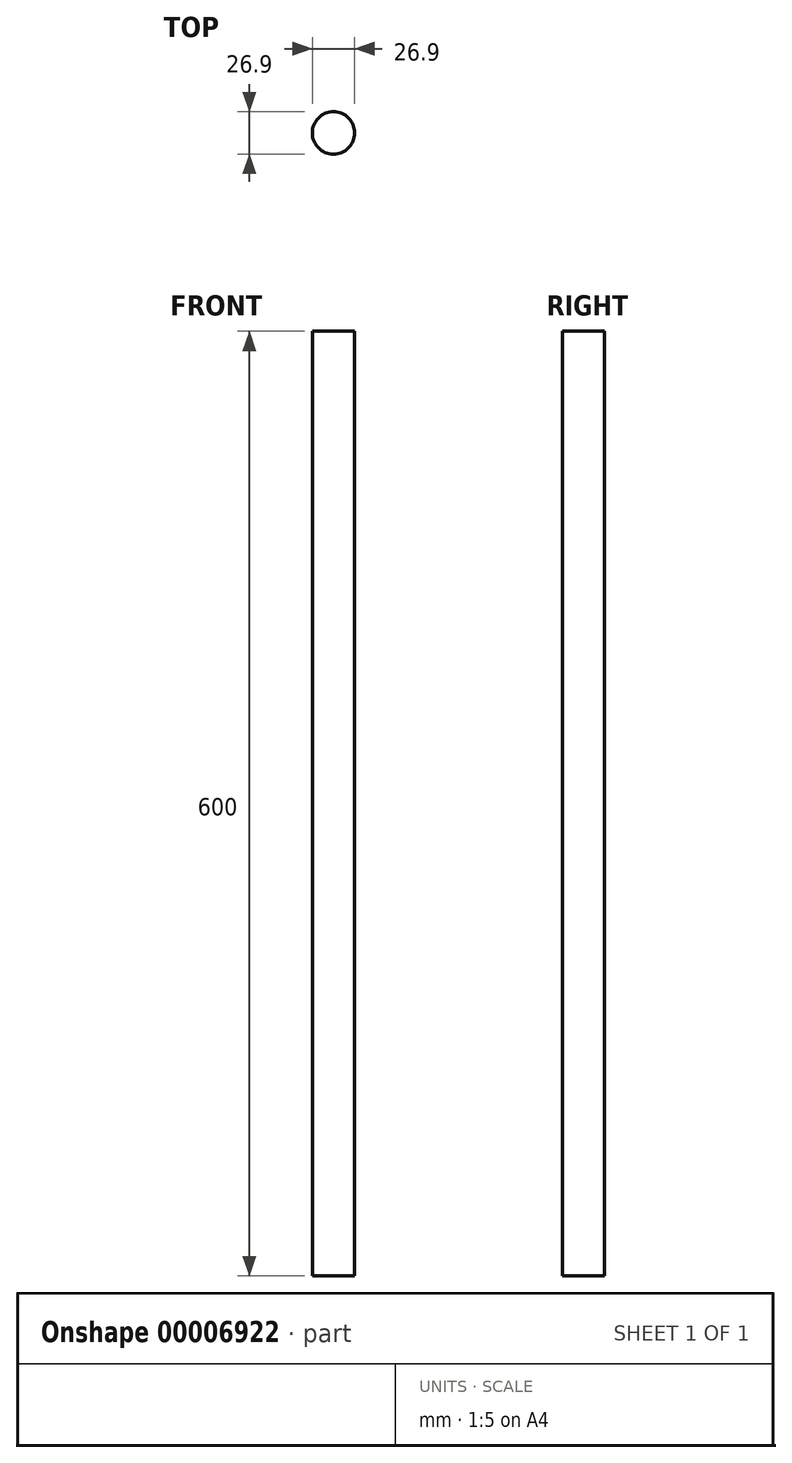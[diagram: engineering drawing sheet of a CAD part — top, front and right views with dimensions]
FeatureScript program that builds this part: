
annotation { "Feature Type Name" : "Feature", "Feature Type Description" : "" }
export const myFeature = defineFeature(function(context is Context, id is Id, definition is map)
    precondition{}
    {
        {
            var Q0;
            Q0=qCreatedBy(makeId("Top.planeOp"),FACE);
            var sketch = newSketch(context, id + "F0", { "sketchPlane" : qUnion([Q0])});
            skCircle(sketch, "E0", {"center": v(0, 0) * mm, "radius": 13.45 * mm});
            skSolve(sketch);
        }
        {
            var Q0;
            Q0=makeQuery(id+"F0.imprint","IMPRINT",FACE,{"disambiguationData":[TD([[makeQuery(id+"F0.imprint","IMPRINT",EDGE,{"derivedFrom":sQuery(id+"F0.wireOp",EDGE,"E0")}),1.0]])]});
            extrude(context, id + "F1", {"entities" : qUnion([Q0]), "depth" : (600) * mm});
        }
    });
